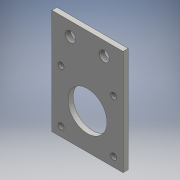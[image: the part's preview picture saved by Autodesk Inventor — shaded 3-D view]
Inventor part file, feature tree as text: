
AUTODESK INVENTOR PART (.ipt)
format: ipt  version: 2016 (Build 200138000, 138)  size: 134,144 bytes
history: native  units: mm
features: extrude x4, sketch x4, projected_geometry x1
ambient origin geometry x8: Origin, YZ Plane, XZ Plane, XY Plane, X Axis, Y Axis, Z Axis, Center Point
bodies: Body1 (feature_tree)
feature tree (9):
  extrude  "拉伸2"  Depth=42.0mm
  extrude  "拉伸6"  Depth=3.0mm
  extrude  "拉伸13"  Depth=15.5mm
  extrude  "拉伸15"  Depth=10.0mm
  sketch  "草图2"  dims[d3=42.0mm d4=42.0mm]
  sketch  "草图7"  dims[d5=3.0mm d6=0.0mm d17=23.0mm]
  sketch  "草图14"  dims[d18=3.5mm d19=15.5mm]
  projected_geometry  "投影回路5"
  sketch  "草图15"  dims[d20=15.5mm d21=15.5mm d22=15.5mm d23=3.0mm d24=0.0mm d49=20.0mm d50=0.0mm d51=6.0mm d52=10.0mm d53=8.0mm d58=10.0mm d59=0.0mm]
